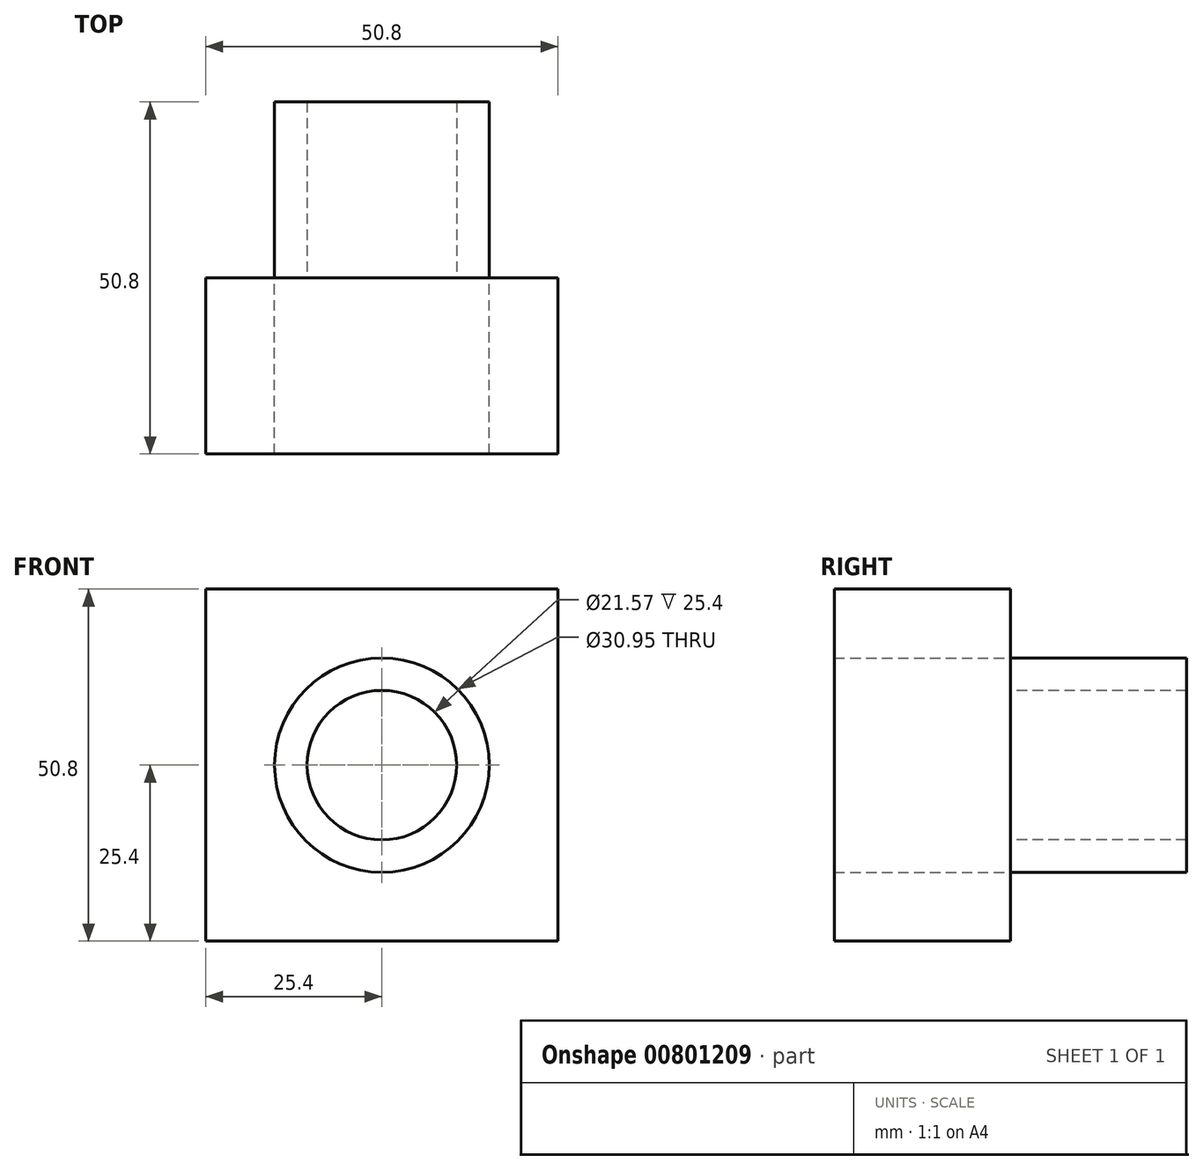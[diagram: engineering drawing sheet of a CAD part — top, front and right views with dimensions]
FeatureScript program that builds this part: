
annotation { "Feature Type Name" : "Feature", "Feature Type Description" : "" }
export const myFeature = defineFeature(function(context is Context, id is Id, definition is map)
    precondition{}
    {
        {
            var Q0;
            Q0=qCreatedBy(makeId("Front.planeOp"),FACE);
            var sketch = newSketch(context, id + "F0", { "sketchPlane" : qUnion([Q0])});
            skLineSegment(sketch, "E0.bottom", {"start": v(0, 0) * mm, "end": v(50.8, 0) * mm});
            skLineSegment(sketch, "E0.top", {"start": v(0, 50.8) * mm, "end": v(50.8, 50.8) * mm});
            skLineSegment(sketch, "E0.left", {"start": v(0, 0) * mm, "end": v(0, 50.8) * mm});
            skLineSegment(sketch, "E0.right", {"start": v(50.8, 0) * mm, "end": v(50.8, 50.8) * mm});
            skCircle(sketch, "E1", {"center": v(25.4, 25.4) * mm, "radius": 10.78 * mm});
            skPoint(sketch, "E2.trimOffspring.end.orphan", {"position": v(0, 25.4) * mm});
            skPoint(sketch, "E3.start.orphan", {"position": v(25.4, 0) * mm});
            skPoint(sketch, "E4.start.orphan", {"position": v(50.8, 25.4) * mm});
            skPoint(sketch, "E5.trimOffspring.end.orphan", {"position": v(25.4, 50.8) * mm});
            skCircle(sketch, "E6", {"center": v(25.4, 25.4) * mm, "radius": 15.47 * mm});
            skSolve(sketch);
        }
        {
            var Q0;
            Q0 = qSketchRegion(id + "F0", true);
            extrude(context, id + "F1", {"entities" : qUnion([Q0]), "depth" : 25.4 * mm, "offsetDistance" : 25.4 * mm});
        }
        {
            var Q0;
            Q0=makeQuery(id+"F0.imprint","IMPRINT",FACE,{"disambiguationData":[TD([[makeQuery(id+"F0.imprint","IMPRINT",EDGE,{"derivedFrom":sQuery(id+"F0.wireOp",EDGE,"E1")}),-1.0]])]});
            extrude(context, id + "F2", {"entities" : qUnion([Q0]), "operationType" : NewBodyOperationType.ADD, "oppositeDirection" : true, "depth" : 25.4 * mm, "offsetDistance" : 25.4 * mm});
        }
    });
